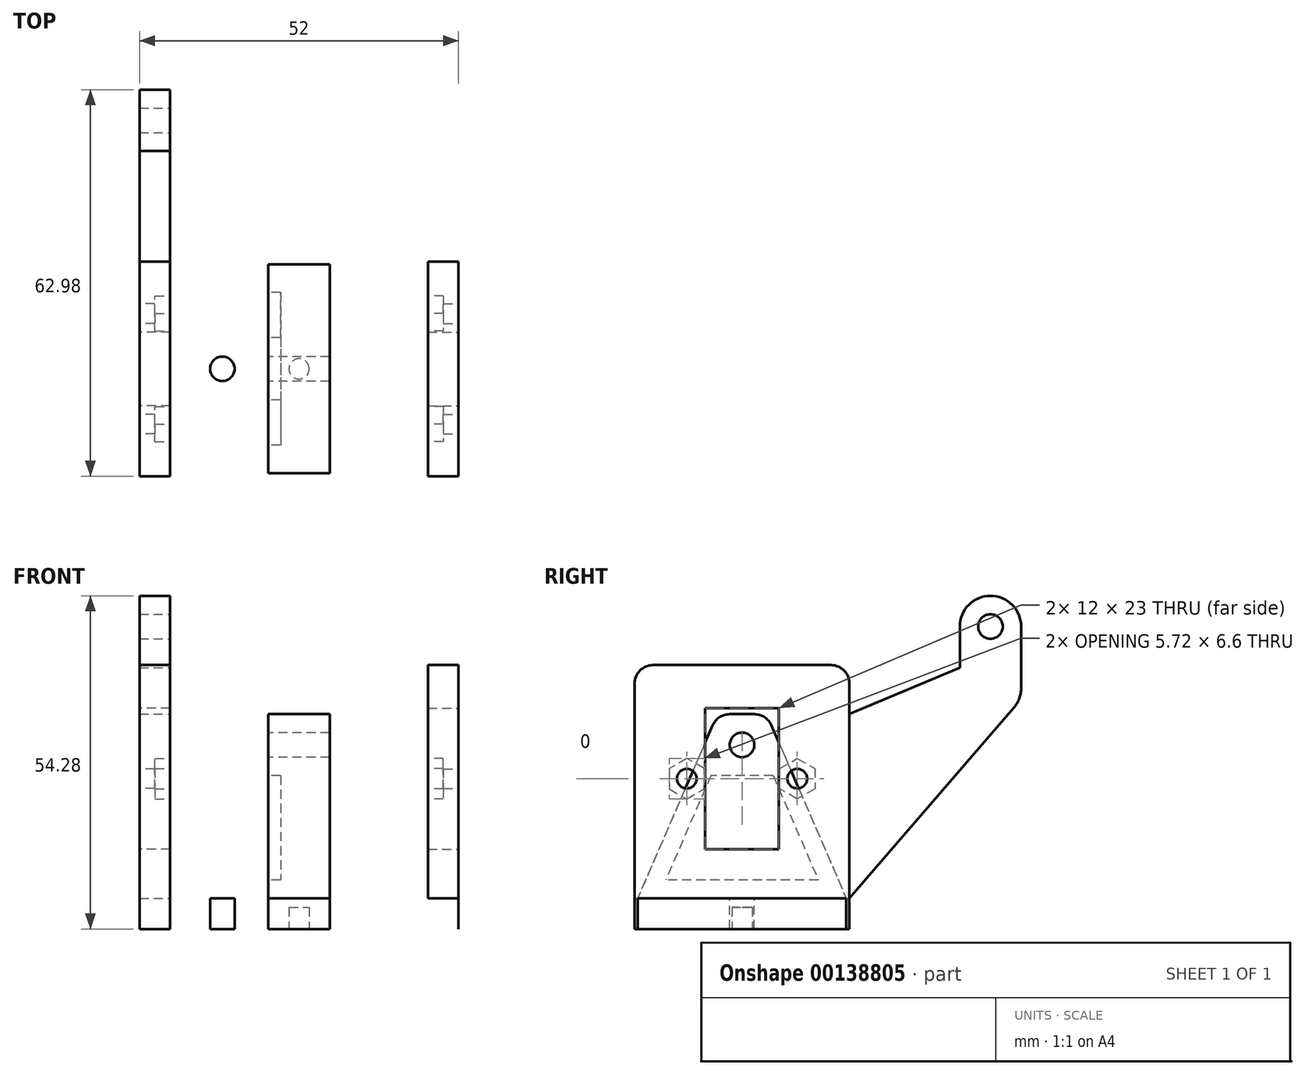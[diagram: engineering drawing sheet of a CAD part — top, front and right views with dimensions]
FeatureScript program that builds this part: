
annotation { "Feature Type Name" : "Feature", "Feature Type Description" : "" }
export const myFeature = defineFeature(function(context is Context, id is Id, definition is map)
    precondition{}
    {
        {
            var Q0;
            Q0=qCreatedBy(makeId("Top.planeOp"),FACE);
            var sketch = newSketch(context, id + "F0", { "sketchPlane" : qUnion([Q0])});
            skLineSegment(sketch, "E0.bottom", {"start": v(-23, 20) * mm, "end": v(23, 20) * mm});
            skLineSegment(sketch, "E0.top", {"start": v(-23, -20) * mm, "end": v(23, -20) * mm});
            skLineSegment(sketch, "E0.left", {"start": v(-26, 17) * mm, "end": v(-26, -17) * mm});
            skLineSegment(sketch, "E0.right", {"start": v(26, 17) * mm, "end": v(26, -17) * mm});
            skPoint(sketch, "E0.middle", {"position": v(0, 0) * mm});
            skPoint(sketch, "E1.visualSharp", {"position": v(-26, 20) * mm});
            skArc(sketch, "E1.filletArc", {"start": v(-23, 20) * mm, "mid": v(-25.12, 19.12) * mm, "end": v(-26, 17) * mm});
            skPoint(sketch, "E2.visualSharp", {"position": v(-26, -20) * mm});
            skArc(sketch, "E2.filletArc", {"start": v(-26, -17) * mm, "mid": v(-25.12, -19.12) * mm, "end": v(-23, -20) * mm});
            skPoint(sketch, "E3.visualSharp", {"position": v(26, -20) * mm});
            skArc(sketch, "E3.filletArc", {"start": v(23, -20) * mm, "mid": v(25.12, -19.12) * mm, "end": v(26, -17) * mm});
            skPoint(sketch, "E4.visualSharp", {"position": v(26, 20) * mm});
            skArc(sketch, "E4.filletArc", {"start": v(26, 17) * mm, "mid": v(25.12, 19.12) * mm, "end": v(23, 20) * mm});
            skSolve(sketch);
        }
        {
            var Q0;
            Q0=qSketchRegion(id+"F0",true);
            extrude(context, id + "F1", {"entities" : qUnion([Q0]), "depth" : 5 * mm});
        }
        {
            var Q0;
            Q0=makeQuery(id+"F1.opExtrude","CAP_FACE",FACE,{"disambiguationData":[OSD([sQuery(id+"F0.wireOp",EDGE,"E0.bottom"),sQuery(id+"F0.wireOp",EDGE,"E0.top"),sQuery(id+"F0.wireOp",EDGE,"E0.left"),sQuery(id+"F0.wireOp",EDGE,"E0.right"),sQuery(id+"F0.wireOp",EDGE,"E1.filletArc"),sQuery(id+"F0.wireOp",EDGE,"E2.filletArc"),sQuery(id+"F0.wireOp",EDGE,"E3.filletArc"),sQuery(id+"F0.wireOp",EDGE,"E4.filletArc")])],"isStart":true});
            var sketch = newSketch(context, id + "F2", { "sketchPlane" : qUnion([Q0])});
            skCircle(sketch, "E5", {"center": v(0, 0) * mm, "radius": 1.65 * mm});
            skSolve(sketch);
        }
        {
            var Q0;
            Q0=qSketchRegion(id+"F2",true);
            extrude(context, id + "F3", {"entities" : qUnion([Q0]), "operationType" : NewBodyOperationType.REMOVE, "oppositeDirection" : true, "depth" : 3.5 * mm});
        }
        {
            var Q0;
            Q0=qCreatedBy(makeId("Right.planeOp"),FACE);
            var sketch = newSketch(context, id + "F4", { "sketchPlane" : qUnion([Q0])});
            skLineSegment(sketch, "E6.0", {"start": v(17, 5) * mm, "end": v(-17, 5) * mm});
            skLineSegment(sketch, "E7", {"start": v(0, 5) * mm, "end": v(0, 35) * mm});
            skPoint(sketch, "E7.endSnap0", {"position": v(0, 5) * mm});
            skLineSegment(sketch, "E8", {"start": v(2.03, 35) * mm, "end": v(-2.03, 35) * mm});
            skLineSegment(sketch, "E9", {"start": v(4.78, 33.2) * mm, "end": v(17, 5) * mm});
            skLineSegment(sketch, "E10", {"start": v(-4.78, 33.2) * mm, "end": v(-17, 5) * mm});
            skPoint(sketch, "E11.visualSharp", {"position": v(4, 35) * mm});
            skArc(sketch, "E11.filletArc", {"start": v(4.78, 33.2) * mm, "mid": v(3.68, 34.5) * mm, "end": v(2.03, 35) * mm});
            skPoint(sketch, "E12.visualSharp", {"position": v(-4, 35) * mm});
            skArc(sketch, "E12.filletArc", {"start": v(-2.03, 35) * mm, "mid": v(-3.68, 34.5) * mm, "end": v(-4.78, 33.2) * mm});
            skSolve(sketch);
        }
        {
            var Q0;
            Q0=qSketchRegion(id+"F4",true);
            extrude(context, id + "F5", {"entities" : qUnion([Q0]), "operationType" : NewBodyOperationType.ADD, "depth" : 5 * mm, "hasSecondDirection" : true, "secondDirectionOppositeDirection" : true, "secondDirectionDepth" : 5 * mm});
        }
        {
            var Q0;
            Q0=makeQuery(id+"F1.opExtrude","SWEPT_FACE",FACE,{"disambiguationData":[OSD([sQuery(id+"F0.wireOp",EDGE,"E0.right")])]});
            var sketch = newSketch(context, id + "F6", { "sketchPlane" : qUnion([Q0])});
            skLineSegment(sketch, "E13.bottom", {"start": v(17.5, 0) * mm, "end": v(-17.5, 0) * mm});
            skLineSegment(sketch, "E13.top", {"start": v(14.5, 43) * mm, "end": v(-14.5, 43) * mm});
            skLineSegment(sketch, "E13.left", {"start": v(17.5, 0) * mm, "end": v(17.5, 40) * mm});
            skLineSegment(sketch, "E13.right", {"start": v(-17.5, 0) * mm, "end": v(-17.5, 40) * mm});
            skLineSegment(sketch, "E14", {"start": v(0, 0) * mm, "end": v(0, 49) * mm, "construction": true});
            skPoint(sketch, "E15.visualSharp", {"position": v(17.5, 43) * mm});
            skArc(sketch, "E15.filletArc", {"start": v(17.5, 40) * mm, "mid": v(16.62, 42.12) * mm, "end": v(14.5, 43) * mm});
            skPoint(sketch, "E16.visualSharp", {"position": v(-17.5, 43) * mm});
            skArc(sketch, "E16.filletArc", {"start": v(-14.5, 43) * mm, "mid": v(-16.62, 42.12) * mm, "end": v(-17.5, 40) * mm});
            skLineSegment(sketch, "E17.bottom", {"start": v(6, 36) * mm, "end": v(-6, 36) * mm});
            skLineSegment(sketch, "E17.top", {"start": v(6, 13) * mm, "end": v(-6, 13) * mm});
            skLineSegment(sketch, "E17.left", {"start": v(6, 36) * mm, "end": v(6, 13) * mm});
            skLineSegment(sketch, "E17.right", {"start": v(-6, 36) * mm, "end": v(-6, 13) * mm});
            skPoint(sketch, "E17.middle", {"position": v(0, 24.5) * mm});
            skLineSegment(sketch, "E18", {"start": v(-17.5, 24.5) * mm, "end": v(17.5, 24.5) * mm, "construction": true});
            skCircle(sketch, "E19", {"center": v(-9, 24.5) * mm, "radius": 1.6 * mm});
            skCircle(sketch, "E20.MirrorC", {"center": v(9, 24.5) * mm, "radius": 1.6 * mm});
            skSolve(sketch);
        }
        {
            var Q0;
            Q0=makeQuery(id+"F6.imprint","IMPRINT",FACE,{"disambiguationData":[TD([[makeQuery(id+"F6.imprint","IMPRINT",EDGE,{"derivedFrom":sQuery(id+"F6.wireOp",EDGE,"E13.top")}),1.0]])]});
            extrude(context, id + "F7", {"entities" : qUnion([Q0]), "oppositeDirection" : true, "depth" : 5 * mm});
        }
        {
            var Q0;
            Q0=makeQuery(id+"F7.opExtrude","CAP_FACE",FACE,{"disambiguationData":[OSD([sQuery(id+"F0.wireOp",EDGE,"E0.right"),sQuery(id+"F0.wireOp",EDGE,"E3.filletArc"),sQuery(id+"F0.wireOp",EDGE,"E4.filletArc"),sQuery(id+"F6.wireOp",EDGE,"E13.bottom"),sQuery(id+"F6.wireOp",EDGE,"E13.top"),sQuery(id+"F6.wireOp",EDGE,"E13.left"),sQuery(id+"F6.wireOp",EDGE,"E13.right"),sQuery(id+"F6.wireOp",EDGE,"E15.filletArc"),sQuery(id+"F6.wireOp",EDGE,"E16.filletArc"),sQuery(id+"F6.wireOp",EDGE,"E17.bottom"),sQuery(id+"F6.wireOp",EDGE,"E17.top"),sQuery(id+"F6.wireOp",EDGE,"E17.left"),sQuery(id+"F6.wireOp",EDGE,"E17.right"),sQuery(id+"F6.wireOp",EDGE,"E19"),sQuery(id+"F6.wireOp",EDGE,"E20.MirrorC")])],"isStart":false});
            var sketch = newSketch(context, id + "F8", { "sketchPlane" : qUnion([Q0])});
            skLineSegment(sketch, "E21", {"start": v(0, 5) * mm, "end": v(0, 43) * mm, "construction": true});
            skCircle(sketch, "E22.cCircle", {"center": v(9, 24.5) * mm, "radius": 2.86 * mm, "construction": true});
            skLineSegment(sketch, "E22.0", {"start": v(9, 27.8) * mm, "end": v(11.86, 26.15) * mm});
            skLineSegment(sketch, "E22.1", {"start": v(11.86, 26.15) * mm, "end": v(11.86, 22.85) * mm});
            skLineSegment(sketch, "E22.2", {"start": v(11.86, 22.85) * mm, "end": v(9, 21.2) * mm});
            skLineSegment(sketch, "E22.3", {"start": v(9, 21.2) * mm, "end": v(6.14, 22.85) * mm});
            skLineSegment(sketch, "E22.4", {"start": v(6.14, 22.85) * mm, "end": v(6.14, 26.15) * mm});
            skLineSegment(sketch, "E22.5", {"start": v(6.14, 26.15) * mm, "end": v(9, 27.8) * mm});
            skPoint(sketch, "E22.0.midPoint", {"position": v(10.43, 26.98) * mm});
            skLineSegment(sketch, "E23.MirrorCS", {"start": v(-9, 21.2) * mm, "end": v(-6.14, 22.85) * mm});
            skLineSegment(sketch, "E24.MirrorCS", {"start": v(-6.14, 22.85) * mm, "end": v(-6.14, 26.15) * mm});
            skCircle(sketch, "E25.MirrorC", {"center": v(-9, 24.5) * mm, "radius": 2.86 * mm, "construction": true});
            skLineSegment(sketch, "E26.MirrorCS", {"start": v(-6.14, 26.15) * mm, "end": v(-9, 27.8) * mm});
            skLineSegment(sketch, "E27.MirrorCS", {"start": v(-9, 27.8) * mm, "end": v(-11.86, 26.15) * mm});
            skLineSegment(sketch, "E28.MirrorCS", {"start": v(-11.86, 22.85) * mm, "end": v(-9, 21.2) * mm});
            skLineSegment(sketch, "E29.MirrorCS", {"start": v(-11.86, 26.15) * mm, "end": v(-11.86, 22.85) * mm});
            skSolve(sketch);
        }
        {
            var Q0;
            Q0=qSketchRegion(id+"F8",true);
            extrude(context, id + "F9", {"entities" : qUnion([Q0]), "operationType" : NewBodyOperationType.REMOVE, "oppositeDirection" : true, "depth" : 2.5 * mm});
        }
        {
            var Q0;
            Q0=makeQuery(id+"F7.opExtrude","SWEPT_BODY",BODY,{"disambiguationData":[OSD([sQuery(id+"F0.wireOp",EDGE,"E0.right"),sQuery(id+"F0.wireOp",EDGE,"E3.filletArc"),sQuery(id+"F0.wireOp",EDGE,"E4.filletArc"),sQuery(id+"F6.wireOp",EDGE,"E13.bottom"),sQuery(id+"F6.wireOp",EDGE,"E13.top"),sQuery(id+"F6.wireOp",EDGE,"E13.left"),sQuery(id+"F6.wireOp",EDGE,"E13.right"),sQuery(id+"F6.wireOp",EDGE,"E15.filletArc"),sQuery(id+"F6.wireOp",EDGE,"E16.filletArc")])]});
            transform(context, id + "F10", {"entities" : qUnion([Q0]), "transformType" : TransformType.TRANSLATION_3D, "dx" : -47 * mm, "dy" : 0 * mm, "dz" : 0 * mm, "makeCopy" : true});
        }
        {
            var Q0;
            Q0=makeQuery(id+"F10.opPattern","COPY",FACE,{"derivedFrom":makeQuery(id+"F7.opExtrude","CAP_FACE",FACE,{"disambiguationData":[OSD([sQuery(id+"F0.wireOp",EDGE,"E0.right"),sQuery(id+"F0.wireOp",EDGE,"E3.filletArc"),sQuery(id+"F0.wireOp",EDGE,"E4.filletArc"),sQuery(id+"F6.wireOp",EDGE,"E13.bottom"),sQuery(id+"F6.wireOp",EDGE,"E13.top"),sQuery(id+"F6.wireOp",EDGE,"E13.left"),sQuery(id+"F6.wireOp",EDGE,"E13.right"),sQuery(id+"F6.wireOp",EDGE,"E15.filletArc"),sQuery(id+"F6.wireOp",EDGE,"E16.filletArc"),sQuery(id+"F6.wireOp",EDGE,"E17.bottom"),sQuery(id+"F6.wireOp",EDGE,"E17.top"),sQuery(id+"F6.wireOp",EDGE,"E17.left"),sQuery(id+"F6.wireOp",EDGE,"E17.right"),sQuery(id+"F6.wireOp",EDGE,"E19"),sQuery(id+"F6.wireOp",EDGE,"E20.MirrorC")])],"isStart":false}),"instanceName":"1"});
            var Q1;
            Q1=makeQuery(id+"F10.opPattern","COPY",FACE,{"derivedFrom":makeQuery(id+"F7.opExtrude","CAP_FACE",FACE,{"disambiguationData":[OSD([sQuery(id+"F0.wireOp",EDGE,"E0.right"),sQuery(id+"F0.wireOp",EDGE,"E3.filletArc"),sQuery(id+"F0.wireOp",EDGE,"E4.filletArc"),sQuery(id+"F6.wireOp",EDGE,"E13.bottom"),sQuery(id+"F6.wireOp",EDGE,"E13.top"),sQuery(id+"F6.wireOp",EDGE,"E13.left"),sQuery(id+"F6.wireOp",EDGE,"E13.right"),sQuery(id+"F6.wireOp",EDGE,"E15.filletArc"),sQuery(id+"F6.wireOp",EDGE,"E16.filletArc"),sQuery(id+"F6.wireOp",EDGE,"E17.bottom"),sQuery(id+"F6.wireOp",EDGE,"E17.top"),sQuery(id+"F6.wireOp",EDGE,"E17.left"),sQuery(id+"F6.wireOp",EDGE,"E17.right"),sQuery(id+"F6.wireOp",EDGE,"E19"),sQuery(id+"F6.wireOp",EDGE,"E20.MirrorC")])],"isStart":true}),"instanceName":"1"});
            cPlane(context, id + "F11", {"entities" : qUnion([Q0, Q1]), "cplaneType" : CPlaneType.MID_PLANE, "offset" : 150 * mm, "width" : 150 * mm, "height" : 150 * mm});
        }
        {
            var Q0;
            Q0=qCreatedBy(id+"F11.planeOp",FACE);
            var sketch = newSketch(context, id + "F12", { "sketchPlane" : qUnion([Q0])});
            skLineSegment(sketch, "E30", {"start": v(0, 0) * mm, "end": v(0, 42.9) * mm, "construction": true});
            skSolve(sketch);
        }
        {
            var Q0;
            Q0=makeQuery(id+"F10.opPattern","COPY",BODY,{"derivedFrom":makeQuery(id+"F7.opExtrude","SWEPT_BODY",BODY,{"disambiguationData":[OSD([sQuery(id+"F0.wireOp",EDGE,"E0.right"),sQuery(id+"F0.wireOp",EDGE,"E3.filletArc"),sQuery(id+"F0.wireOp",EDGE,"E4.filletArc"),sQuery(id+"F6.wireOp",EDGE,"E13.bottom"),sQuery(id+"F6.wireOp",EDGE,"E13.top"),sQuery(id+"F6.wireOp",EDGE,"E13.left"),sQuery(id+"F6.wireOp",EDGE,"E13.right"),sQuery(id+"F6.wireOp",EDGE,"E15.filletArc"),sQuery(id+"F6.wireOp",EDGE,"E16.filletArc"),sQuery(id+"F6.wireOp",EDGE,"E17.bottom"),sQuery(id+"F6.wireOp",EDGE,"E17.top"),sQuery(id+"F6.wireOp",EDGE,"E17.left"),sQuery(id+"F6.wireOp",EDGE,"E17.right"),sQuery(id+"F6.wireOp",EDGE,"E19"),sQuery(id+"F6.wireOp",EDGE,"E20.MirrorC")])]}),"instanceName":"1"});
            var Q1;
            Q1=sQuery(id+"F12.wireOp",EDGE,"E30");
            transform(context, id + "F13", {"entities" : qUnion([Q0]), "transformType" : TransformType.ROTATION, "transformAxis" : qUnion([Q1]), "angle" : 180 * degree, "makeCopy" : false});
        }
        {
            var Q0;
            Q0=makeQuery(id+"F5.opExtrude","CAP_FACE",FACE,{"disambiguationData":[OSD([sQuery(id+"F4.wireOp",EDGE,"E6.0"),sQuery(id+"F4.wireOp",EDGE,"E8"),sQuery(id+"F4.wireOp",EDGE,"E9"),sQuery(id+"F4.wireOp",EDGE,"E10"),sQuery(id+"F4.wireOp",EDGE,"E11.filletArc"),sQuery(id+"F4.wireOp",EDGE,"E12.filletArc")])],"isStart":true});
            var sketch = newSketch(context, id + "F14", { "sketchPlane" : qUnion([Q0])});
            skCircle(sketch, "E31", {"center": v(0, 30) * mm, "radius": 2 * mm});
            skSolve(sketch);
        }
        {
            var Q0;
            Q0=makeQuery(id+"F14.imprint","IMPRINT",FACE,{"disambiguationData":[TD([[makeQuery(id+"F14.imprint","IMPRINT",EDGE,{"derivedFrom":sQuery(id+"F14.wireOp",EDGE,"E31")}),1.0]])]});
            extrude(context, id + "F15", {"entities" : qUnion([Q0]), "operationType" : NewBodyOperationType.REMOVE, "oppositeDirection" : true, "depth" : 25 * mm});
        }
        {
            var Q0;
            Q0=makeQuery(id+"F10.opPattern","COPY",FACE,{"derivedFrom":makeQuery(id+"F7.opExtrude","CAP_FACE",FACE,{"disambiguationData":[OSD([sQuery(id+"F0.wireOp",EDGE,"E0.right"),sQuery(id+"F0.wireOp",EDGE,"E3.filletArc"),sQuery(id+"F0.wireOp",EDGE,"E4.filletArc"),sQuery(id+"F6.wireOp",EDGE,"E13.bottom"),sQuery(id+"F6.wireOp",EDGE,"E13.top"),sQuery(id+"F6.wireOp",EDGE,"E13.left"),sQuery(id+"F6.wireOp",EDGE,"E13.right"),sQuery(id+"F6.wireOp",EDGE,"E15.filletArc"),sQuery(id+"F6.wireOp",EDGE,"E16.filletArc"),sQuery(id+"F6.wireOp",EDGE,"E17.bottom"),sQuery(id+"F6.wireOp",EDGE,"E17.top"),sQuery(id+"F6.wireOp",EDGE,"E17.left"),sQuery(id+"F6.wireOp",EDGE,"E17.right"),sQuery(id+"F6.wireOp",EDGE,"E19"),sQuery(id+"F6.wireOp",EDGE,"E20.MirrorC")])],"isStart":false}),"instanceName":"1"});
            var sketch = newSketch(context, id + "F16", { "sketchPlane" : qUnion([Q0])});
            skLineSegment(sketch, "E32.0", {"start": v(17.5, 0) * mm, "end": v(17.5, 5) * mm});
            skLineSegment(sketch, "E33", {"start": v(17.5, 5) * mm, "end": v(17.5, 35) * mm});
            skLineSegment(sketch, "E34", {"start": v(17.5, 35) * mm, "end": v(17.5, 40) * mm});
            skPoint(sketch, "E35", {"position": v(17.5, 20) * mm});
            skLineSegment(sketch, "E36", {"start": v(17.5, 20) * mm, "end": v(40.48, 39.28) * mm, "construction": true});
            skLineSegment(sketch, "E37", {"start": v(44.27, 36.02) * mm, "end": v(17.5, 5) * mm});
            skLineSegment(sketch, "E38", {"start": v(38.54, 43.89) * mm, "end": v(17.5, 35) * mm});
            skLineSegment(sketch, "E39", {"start": v(40.48, 39.28) * mm, "end": v(40.48, 49.28) * mm, "construction": true});
            skLineSegment(sketch, "E40", {"start": v(35.48, 49.28) * mm, "end": v(35.48, 39.28) * mm});
            skLineSegment(sketch, "E41", {"start": v(45.48, 49.28) * mm, "end": v(45.48, 49.28) * mm});
            skLineSegment(sketch, "E42", {"start": v(45.48, 39.28) * mm, "end": v(45.48, 39.28) * mm});
            skLineSegment(sketch, "E43", {"start": v(35.48, 39.28) * mm, "end": v(35.48, 39.28) * mm});
            skArc(sketch, "E44", {"start": v(45.48, 39.28) * mm, "mid": v(40.48, 44.28) * mm, "end": v(35.48, 39.28) * mm, "construction": true});
            skLineSegment(sketch, "E45", {"start": v(45.48, 49.28) * mm, "end": v(45.48, 39.28) * mm});
            skArc(sketch, "E46", {"start": v(35.48, 49.28) * mm, "mid": v(40.48, 44.28) * mm, "end": v(45.48, 49.28) * mm, "construction": true});
            skArc(sketch, "E47", {"start": v(45.48, 49.28) * mm, "mid": v(40.48, 54.28) * mm, "end": v(35.48, 49.28) * mm});
            skArc(sketch, "E48", {"start": v(44.27, 36.02) * mm, "mid": v(45.17, 37.54) * mm, "end": v(45.48, 39.28) * mm});
            skArc(sketch, "E49", {"start": v(35.48, 39.28) * mm, "mid": v(38.74, 34.6) * mm, "end": v(44.27, 36.02) * mm, "construction": true});
            skSolve(sketch);
        }
        {
            var Q0;
            Q0=qSketchRegion(id+"F16",true);
            extrude(context, id + "F17", {"entities" : qUnion([Q0]), "operationType" : NewBodyOperationType.ADD, "oppositeDirection" : true, "depth" : (5) * mm});
        }
        {
            var Q0;
            Q0=makeQuery(id+"F17.boolean.opBoolean","MERGE",FACE,{"derivedFrom":[makeQuery(id+"F10.opPattern","COPY",FACE,{"derivedFrom":makeQuery(id+"F7.opExtrude","CAP_FACE",FACE,{"disambiguationData":[OSD([sQuery(id+"F0.wireOp",EDGE,"E0.right"),sQuery(id+"F0.wireOp",EDGE,"E3.filletArc"),sQuery(id+"F0.wireOp",EDGE,"E4.filletArc"),sQuery(id+"F6.wireOp",EDGE,"E13.bottom"),sQuery(id+"F6.wireOp",EDGE,"E13.top"),sQuery(id+"F6.wireOp",EDGE,"E13.left"),sQuery(id+"F6.wireOp",EDGE,"E13.right"),sQuery(id+"F6.wireOp",EDGE,"E15.filletArc"),sQuery(id+"F6.wireOp",EDGE,"E16.filletArc"),sQuery(id+"F6.wireOp",EDGE,"E17.bottom"),sQuery(id+"F6.wireOp",EDGE,"E17.top"),sQuery(id+"F6.wireOp",EDGE,"E17.left"),sQuery(id+"F6.wireOp",EDGE,"E17.right"),sQuery(id+"F6.wireOp",EDGE,"E19"),sQuery(id+"F6.wireOp",EDGE,"E20.MirrorC")])],"isStart":false}),"instanceName":"1"}),makeQuery(id+"F17.opExtrude","CAP_FACE",FACE,{"disambiguationData":[OSD([sQuery(id+"F16.wireOp",EDGE,"E33"),sQuery(id+"F16.wireOp",EDGE,"E37"),sQuery(id+"F16.wireOp",EDGE,"E38"),sQuery(id+"F16.wireOp",EDGE,"E40"),sQuery(id+"F16.wireOp",EDGE,"E45"),sQuery(id+"F16.wireOp",EDGE,"E47"),sQuery(id+"F16.wireOp",EDGE,"E48")])],"isStart":true})]});
            var sketch = newSketch(context, id + "F18", { "sketchPlane" : qUnion([Q0])});
            skCircle(sketch, "E50", {"center": v(40.48, 49.28) * mm, "radius": 2 * mm});
            skSolve(sketch);
        }
        {
            var Q0;
            Q0=makeQuery(id+"F18.imprint","IMPRINT",FACE,{"disambiguationData":[TD([[makeQuery(id+"F18.imprint","IMPRINT",EDGE,{"derivedFrom":sQuery(id+"F18.wireOp",EDGE,"E50")}),1.0]])]});
            extrude(context, id + "F19", {"entities" : qUnion([Q0]), "operationType" : NewBodyOperationType.REMOVE, "endBound" : BoundingType.THROUGH_ALL, "oppositeDirection" : true, "depth" : 25 * mm});
        }
        {
            var Q0;
            Q0=makeQuery(id+"F1.opExtrude","CAP_FACE",FACE,{"disambiguationData":[OSD([sQuery(id+"F0.wireOp",EDGE,"E0.bottom"),sQuery(id+"F0.wireOp",EDGE,"E0.top"),sQuery(id+"F0.wireOp",EDGE,"E0.left"),sQuery(id+"F0.wireOp",EDGE,"E0.right"),sQuery(id+"F0.wireOp",EDGE,"E1.filletArc"),sQuery(id+"F0.wireOp",EDGE,"E2.filletArc"),sQuery(id+"F0.wireOp",EDGE,"E3.filletArc"),sQuery(id+"F0.wireOp",EDGE,"E4.filletArc")])],"isStart":false});
            var sketch = newSketch(context, id + "F20", { "sketchPlane" : qUnion([Q0])});
            skCircle(sketch, "E51", {"center": v(12.5, 0) * mm, "radius": 2 * mm});
            skCircle(sketch, "E52.MirrorC", {"center": v(-12.5, 0) * mm, "radius": 2 * mm});
            skSolve(sketch);
        }
        {
            var Q0;
            Q0=makeQuery(id+"F20.imprint","IMPRINT",FACE,{"disambiguationData":[TD([[makeQuery(id+"F20.imprint","IMPRINT",EDGE,{"derivedFrom":sQuery(id+"F20.wireOp",EDGE,"E52.MirrorC")}),-1.0]])]});
            var Q1;
            Q1=makeQuery(id+"F20.imprint","IMPRINT",FACE,{"disambiguationData":[TD([[makeQuery(id+"F20.imprint","IMPRINT",EDGE,{"derivedFrom":sQuery(id+"F20.wireOp",EDGE,"E51")}),1.0]])]});
            extrude(context, id + "F21", {"entities" : qUnion([Q0, Q1]), "operationType" : NewBodyOperationType.REMOVE, "endBound" : BoundingType.THROUGH_ALL, "oppositeDirection" : true, "depth" : 25 * mm});
        }
        {
            var Q0;
            Q0=makeQuery(id+"F5.opExtrude","CAP_FACE",FACE,{"disambiguationData":[OSD([sQuery(id+"F4.wireOp",EDGE,"E6.0"),sQuery(id+"F4.wireOp",EDGE,"E8"),sQuery(id+"F4.wireOp",EDGE,"E9"),sQuery(id+"F4.wireOp",EDGE,"E10"),sQuery(id+"F4.wireOp",EDGE,"E11.filletArc"),sQuery(id+"F4.wireOp",EDGE,"E12.filletArc")])],"isStart":true});
            var sketch = newSketch(context, id + "F22", { "sketchPlane" : qUnion([Q0])});
            skLineSegment(sketch, "E53.1", {"start": v(-12.43, 8) * mm, "end": v(12.43, 8) * mm});
            skLineSegment(sketch, "E54", {"start": v(-5.06, 25) * mm, "end": v(5.06, 25) * mm});
            skLineSegment(sketch, "E55", {"start": v(5.06, 25) * mm, "end": v(12.43, 8) * mm});
            skLineSegment(sketch, "E56", {"start": v(-5.06, 25) * mm, "end": v(-12.43, 8) * mm});
            skSolve(sketch);
        }
        {
            var Q0;
            Q0=makeQuery(id+"F22.imprint","IMPRINT",FACE,{"disambiguationData":[TD([[makeQuery(id+"F22.imprint","IMPRINT",EDGE,{"derivedFrom":sQuery(id+"F22.wireOp",EDGE,"E53.1")}),1.0]])]});
            extrude(context, id + "F23", {"entities" : qUnion([Q0]), "operationType" : NewBodyOperationType.REMOVE, "oppositeDirection" : true, "depth" : (2) * mm});
        }
    });
